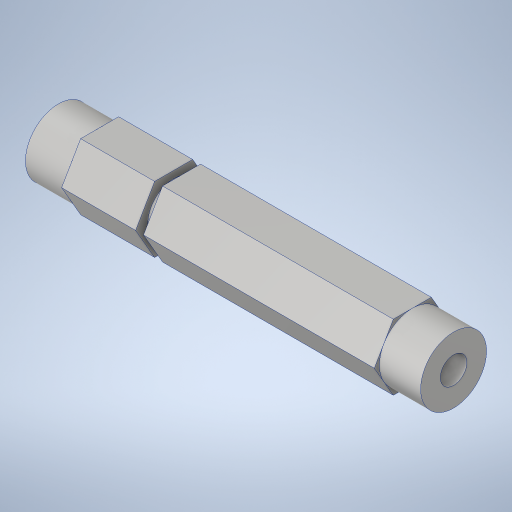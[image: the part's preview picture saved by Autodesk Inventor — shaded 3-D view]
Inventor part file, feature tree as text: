
AUTODESK INVENTOR PART (.ipt)
format: ipt  version: 2023.4 (Build 274418000, 418)  size: 284,672 bytes
history: native  units: in
note: dims shown in document units (in); Inventor stores cm internally (conversion verified against a paired STEP export)
features: sketch x5, extrude x3, projected_geometry x2, hole x1, revolve x1
ambient origin geometry x8: Origin, YZ Plane, XZ Plane, XY Plane, X Axis, Y Axis, Z Axis, Center Point
bodies: Solid1 (feature_tree)
feature tree (12):
  extrude  "Extrusion1"  Depth=2.374in TaperAngle=0.0deg
  extrude  "Extrusion2"  Depth=0.313in TaperAngle=0.0deg
  extrude  "Extrusion3"  Depth=0.313in TaperAngle=0.0deg
  hole  "Hole1"  [1 undecoded]
  revolve  "Revolution1"  [1 undecoded]
  sketch  "Sketch1"  dims[d0=0.5in d1=2.374in d2=0.0in]
  sketch  "Sketch2"  dims[d3=0.5in d4=0.313in d5=0.0in]
  sketch  "Sketch3"  dims[d6=0.5in d7=0.313in d8=0.0in]
  sketch  "Sketch4"  dims[d9=0.201in d10=0.75in d11=0.385in d12=0.25in d13=0.5635in d14=1.0in d15=0.8108in d16=0.392in]
  projected_geometry  "Projected Loop1"
  sketch  "Sketch6"  dims[d17=0.06in d18=0.875in d19=90.0deg]
  projected_geometry  "Project Cut Edges1"
note: 2 required parameter values undecoded (feature->parameter linkage not recoverable at this tier; creation-order binding heuristic only, values carry confidence <= 0.55)